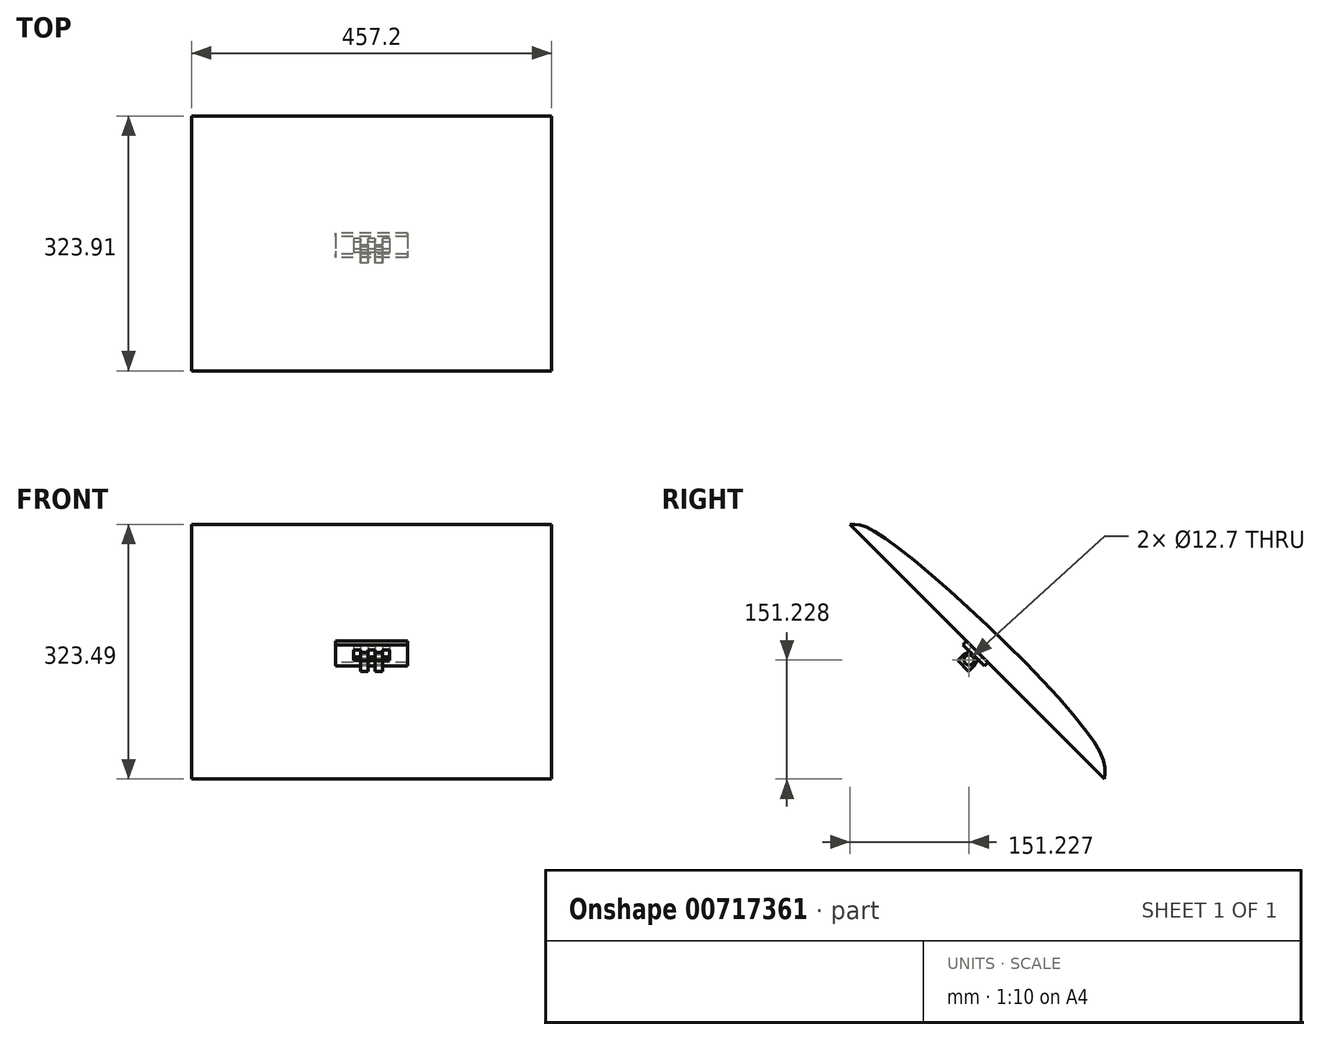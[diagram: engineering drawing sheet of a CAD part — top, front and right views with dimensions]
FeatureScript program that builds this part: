
annotation { "Feature Type Name" : "Feature", "Feature Type Description" : "" }
export const myFeature = defineFeature(function(context is Context, id is Id, definition is map)
    precondition{}
    {
        {
            var Q0;
            Q0=qCreatedBy(makeId("Right.planeOp"),FACE);
            var sketch = newSketch(context, id + "F0", { "sketchPlane" : qUnion([Q0])});
            skLineSegment(sketch, "E0", {"start": v(0, 0) * mm, "end": v(323.29, -323.29) * mm});
            skFitSpline(sketch, "E1", {"points": [v(0, 0) * mm, v(34.26, -10.27) * mm, v(310.43, -276.84) * mm, v(323.29, -323.29) * mm], "startDerivative": vector(129.19, 8.1) * mm, "endDerivative": vector(-16.33, -160.72) * mm});
            skSolve(sketch);
        }
        {
            var Q0;
            Q0 = qSketchRegion(id + "F0", true);
            extrude(context, id + "F1", {"entities" : qUnion([Q0]), "depth" : 457.2 * mm, "offsetDistance" : 25.4 * mm});
        }
        {
            var Q0;
            Q0=makeQuery(id+"F1.opExtrude","SWEPT_FACE",FACE,{"disambiguationData":[OSD([sQuery(id+"F0.wireOp",EDGE,"E0")])]});
            var sketch = newSketch(context, id + "F2", { "sketchPlane" : qUnion([Q0])});
            skLineSegment(sketch, "E2", {"start": v(228.6, 0) * mm, "end": v(228.6, -457.2) * mm, "construction": true});
            skLineSegment(sketch, "E3", {"start": v(0, -228.6) * mm, "end": v(457.2, -228.6) * mm, "construction": true});
            skPoint(sketch, "E4.middle", {"position": v(228.6, -228.6) * mm});
            skLineSegment(sketch, "E5.bottom", {"start": v(274.32, -247.65) * mm, "end": v(182.88, -247.65) * mm});
            skLineSegment(sketch, "E5.top", {"start": v(274.32, -209.55) * mm, "end": v(182.88, -209.55) * mm});
            skLineSegment(sketch, "E5.left", {"start": v(274.32, -247.65) * mm, "end": v(274.32, -209.55) * mm});
            skLineSegment(sketch, "E5.right", {"start": v(182.88, -247.65) * mm, "end": v(182.88, -209.55) * mm});
            skSolve(sketch);
        }
        {
            var Q0;
            Q0=makeQuery(id+"F2.imprint","IMPRINT",FACE,{"disambiguationData":[TD([[makeQuery(id+"F2.imprint","IMPRINT",EDGE,{"derivedFrom":sQuery(id+"F2.wireOp",EDGE,"E5.bottom")}),-1.0]])]});
            extrude(context, id + "F3", {"entities" : qUnion([Q0]), "operationType" : NewBodyOperationType.ADD, "depth" : 6.35 * mm, "offsetDistance" : 25.4 * mm});
        }
        {
            var Q0;
            Q0=makeQuery(id+"F3.opExtrude","CAP_FACE",FACE,{"disambiguationData":[OSD([sQuery(id+"F2.wireOp",EDGE,"E5.bottom"),sQuery(id+"F2.wireOp",EDGE,"E5.top"),sQuery(id+"F2.wireOp",EDGE,"E5.left"),sQuery(id+"F2.wireOp",EDGE,"E5.right")])],"isStart":false});
            var sketch = newSketch(context, id + "F4", { "sketchPlane" : qUnion([Q0])});
            skLineSegment(sketch, "E6", {"start": v(182.88, -228.6) * mm, "end": v(274.32, -228.6) * mm, "construction": true});
            skLineSegment(sketch, "E7", {"start": v(228.6, -209.55) * mm, "end": v(228.6, -247.65) * mm, "construction": true});
            skLineSegment(sketch, "E8.bottom", {"start": v(251.46, -238.12) * mm, "end": v(205.74, -238.12) * mm});
            skLineSegment(sketch, "E8.top", {"start": v(251.46, -219.07) * mm, "end": v(205.74, -219.07) * mm});
            skLineSegment(sketch, "E8.left", {"start": v(251.46, -238.12) * mm, "end": v(251.46, -219.07) * mm});
            skLineSegment(sketch, "E8.right", {"start": v(205.74, -238.12) * mm, "end": v(205.74, -219.07) * mm});
            skPoint(sketch, "E8.middle", {"position": v(228.6, -228.6) * mm});
            skSolve(sketch);
        }
        {
            var Q0;
            Q0=makeQuery(id+"F4.imprint","IMPRINT",FACE,{"disambiguationData":[TD([[makeQuery(id+"F4.imprint","IMPRINT",EDGE,{"derivedFrom":sQuery(id+"F4.wireOp",EDGE,"E8.bottom")}),-1.0]])]});
            extrude(context, id + "F5", {"entities" : qUnion([Q0]), "operationType" : NewBodyOperationType.ADD, "depth" : 19.05 * mm, "offsetDistance" : 25.4 * mm});
        }
        {
            var Q0;
            Q0=makeQuery(id+"F5.opExtrude","CAP_FACE",FACE,{"disambiguationData":[OSD([sQuery(id+"F4.wireOp",EDGE,"E8.bottom"),sQuery(id+"F4.wireOp",EDGE,"E8.top"),sQuery(id+"F4.wireOp",EDGE,"E8.left"),sQuery(id+"F4.wireOp",EDGE,"E8.right")])],"isStart":false});
            var sketch = newSketch(context, id + "F6", { "sketchPlane" : qUnion([Q0])});
            skLineSegment(sketch, "E9", {"start": v(205.74, -219.07) * mm, "end": v(214.88, -219.07) * mm, "construction": true});
            skLineSegment(sketch, "E10", {"start": v(214.88, -219.07) * mm, "end": v(224.03, -219.07) * mm, "construction": true});
            skLineSegment(sketch, "E11", {"start": v(224.03, -219.07) * mm, "end": v(233.17, -219.07) * mm, "construction": true});
            skLineSegment(sketch, "E12", {"start": v(233.17, -219.07) * mm, "end": v(242.32, -219.07) * mm, "construction": true});
            skLineSegment(sketch, "E13.bottom", {"start": v(205.74, -219.07) * mm, "end": v(214.88, -219.07) * mm});
            skLineSegment(sketch, "E13.top", {"start": v(205.74, -238.12) * mm, "end": v(214.88, -238.12) * mm});
            skLineSegment(sketch, "E13.left", {"start": v(205.74, -219.07) * mm, "end": v(205.74, -238.12) * mm});
            skLineSegment(sketch, "E13.right", {"start": v(214.88, -219.07) * mm, "end": v(214.88, -238.12) * mm});
            skLineSegment(sketch, "E14.bottom", {"start": v(224.03, -219.07) * mm, "end": v(233.17, -219.07) * mm});
            skLineSegment(sketch, "E14.top", {"start": v(224.03, -238.12) * mm, "end": v(233.17, -238.12) * mm});
            skLineSegment(sketch, "E14.left", {"start": v(224.03, -219.07) * mm, "end": v(224.03, -238.12) * mm});
            skLineSegment(sketch, "E14.right", {"start": v(233.17, -219.07) * mm, "end": v(233.17, -238.12) * mm});
            skLineSegment(sketch, "E15.bottom", {"start": v(242.32, -219.07) * mm, "end": v(251.46, -219.07) * mm});
            skLineSegment(sketch, "E15.top", {"start": v(242.32, -238.12) * mm, "end": v(251.46, -238.12) * mm});
            skLineSegment(sketch, "E15.left", {"start": v(242.32, -219.07) * mm, "end": v(242.32, -238.12) * mm});
            skLineSegment(sketch, "E15.right", {"start": v(251.46, -219.07) * mm, "end": v(251.46, -238.12) * mm});
            skSolve(sketch);
        }
        {
            var Q0;
            Q0=makeQuery(id+"F6.imprint","IMPRINT",FACE,{"disambiguationData":[TD([[makeQuery(id+"F6.imprint","IMPRINT",EDGE,{"derivedFrom":sQuery(id+"F6.wireOp",EDGE,"E13.bottom")}),1.0]])]});
            var Q1;
            Q1=makeQuery(id+"F6.imprint","IMPRINT",FACE,{"disambiguationData":[TD([[makeQuery(id+"F6.imprint","IMPRINT",EDGE,{"derivedFrom":sQuery(id+"F6.wireOp",EDGE,"E14.bottom")}),1.0]])]});
            var Q2;
            Q2=makeQuery(id+"F6.imprint","IMPRINT",FACE,{"disambiguationData":[TD([[makeQuery(id+"F6.imprint","IMPRINT",EDGE,{"derivedFrom":sQuery(id+"F6.wireOp",EDGE,"E15.bottom")}),1.0]])]});
            extrude(context, id + "F7", {"entities" : qUnion([Q0, Q1, Q2]), "operationType" : NewBodyOperationType.REMOVE, "oppositeDirection" : true, "depth" : 25.4 * mm, "offsetDistance" : 25.4 * mm});
        }
        {
            var Q0;
            Q0=makeQuery(id+"F7.boolean.opBoolean","COPY",FACE,{"derivedFrom":makeQuery(id+"F7.opExtrude","SWEPT_FACE",FACE,{"disambiguationData":[OSD([sQuery(id+"F6.wireOp",EDGE,"E15.left")])]})});
            var sketch = newSketch(context, id + "F8", { "sketchPlane" : qUnion([Q0])});
            skLineSegment(sketch, "E16", {"start": v(143.68, -179.6) * mm, "end": v(151.23, -172.06) * mm, "construction": true});
            skCircle(sketch, "E17", {"center": v(151.23, -172.06) * mm, "radius": 9.53 * mm});
            skLineSegment(sketch, "E18", {"start": v(150.42, -159.4) * mm, "end": v(153.96, -162.94) * mm});
            skLineSegment(sketch, "E19", {"start": v(163.89, -172.87) * mm, "end": v(160.35, -169.33) * mm});
            skSolve(sketch);
        }
        {
            var Q0;
            {var subQ0=sQuery(id+"F8.wireOp",EDGE,"E18");Q0=makeQuery(id+"F8.imprint","IMPRINT",FACE,{"disambiguationData":[TD([[makeQuery(id+"F8.imprint","IMPRINT",EDGE,{"derivedFrom":subQ0}),-1.0]])]});}
            var Q1;
            {var subQ0=sQuery(id+"F8.wireOp",EDGE,"E19");Q1=makeQuery(id+"F8.imprint","IMPRINT",FACE,{"disambiguationData":[TD([[makeQuery(id+"F8.imprint","IMPRINT",EDGE,{"derivedFrom":subQ0}),1.0]])]});}
            var Q2;
            {var subQ2=sQuery(id+"F6.wireOp",EDGE,"E15.left");var subQ9=makeQuery(id+"F7.boolean.opBoolean","COPY",EDGE,{"derivedFrom":makeQuery(id+"F7.opExtrude","CAP_EDGE",EDGE,{"disambiguationData":[OSD([subQ2])],"isStart":true})});Q2=makeQuery(id+"F8.imprint","IMPRINT",FACE,{"disambiguationData":[TD([[makeQuery(id+"F8.imprint","IMPRINT",EDGE,{"derivedFrom":subQ9}),1.0]])]});}
            extrude(context, id + "F9", {"entities" : qUnion([Q0, Q1, Q2]), "operationType" : NewBodyOperationType.REMOVE, "oppositeDirection" : true, "depth" : 27.94 * mm, "offsetDistance" : 25.4 * mm});
        }
        {
            var Q0;
            Q0=makeQuery(id+"F7.boolean.opBoolean","COPY",FACE,{"derivedFrom":makeQuery(id+"F7.opExtrude","SWEPT_FACE",FACE,{"disambiguationData":[OSD([sQuery(id+"F6.wireOp",EDGE,"E13.right")])]})});
            var sketch = newSketch(context, id + "F10", { "sketchPlane" : qUnion([Q0])});
            skLineSegment(sketch, "E20", {"start": v(-144.62, -165.2) * mm, "end": v(-157.84, -178.92) * mm, "construction": true});
            skLineSegment(sketch, "E21", {"start": v(-149.96, -162.62) * mm, "end": v(-152.5, -181.5) * mm, "construction": true});
            skCircle(sketch, "E22", {"center": v(-151.23, -172.06) * mm, "radius": 6.35 * mm});
            skSolve(sketch);
        }
        {
            var Q0;
            Q0=makeQuery(id+"F10.imprint","IMPRINT",FACE,{"disambiguationData":[TD([[makeQuery(id+"F10.imprint","IMPRINT",EDGE,{"derivedFrom":sQuery(id+"F10.wireOp",EDGE,"E22")}),1.0]])]});
            extrude(context, id + "F11", {"entities" : qUnion([Q0]), "operationType" : NewBodyOperationType.REMOVE, "oppositeDirection" : true, "depth" : 50.8 * mm, "offsetDistance" : 25.4 * mm});
        }
    });
